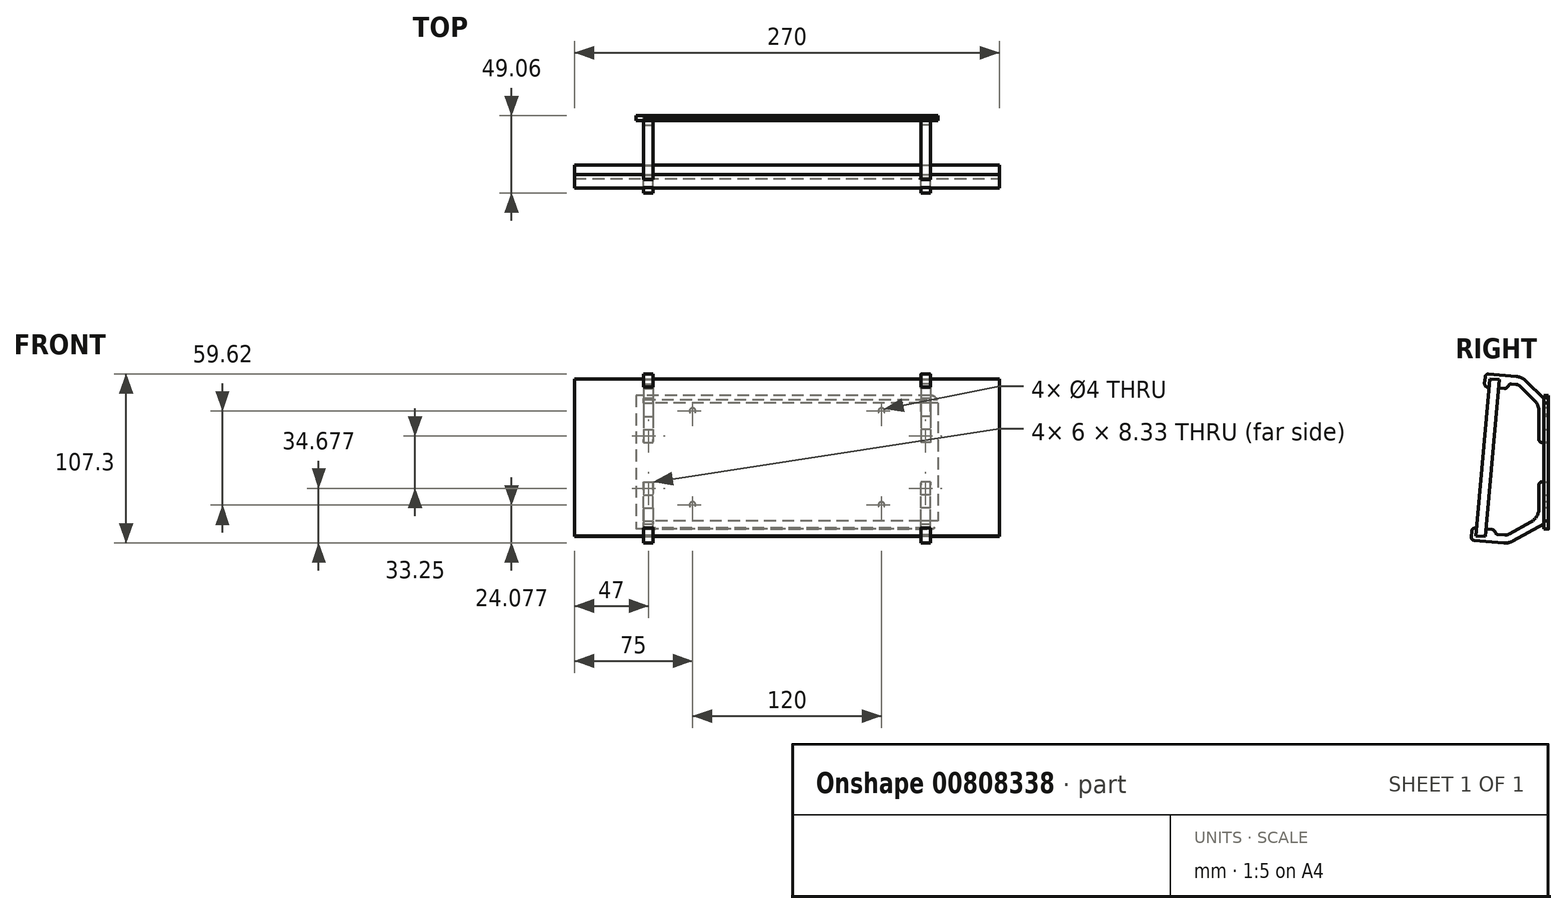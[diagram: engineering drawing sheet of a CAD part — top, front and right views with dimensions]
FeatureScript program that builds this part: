
annotation { "Feature Type Name" : "Feature", "Feature Type Description" : "" }
export const myFeature = defineFeature(function(context is Context, id is Id, definition is map)
    precondition{}
    {
        {
            var Q0;
            Q0=qCreatedBy(makeId("Front.planeOp"),FACE);
            var sketch = newSketch(context, id + "F0", { "sketchPlane" : qUnion([Q0])});
            skLineSegment(sketch, "E0", {"start": v(-49.98, 0) * mm, "end": v(35.18, 0) * mm});
            skSolve(sketch);
        }
        {
            var Q0;
            Q0=qCreatedBy(makeId("Front.planeOp"),FACE);
            var Q1;
            Q1=sQuery(id+"F0.wireOp",EDGE,"E0");
            cPlane(context, id + "F1", {"entities" : qUnion([Q0, Q1]), "cplaneType" : CPlaneType.LINE_ANGLE, "offset" : 25 * mm, "angle" : 5 * degree, "oppositeDirection" : true, "width" : 150 * mm, "height" : 150 * mm});
        }
        {
            var Q0;
            Q0=qCreatedBy(id+"F1.planeOp",FACE);
            var sketch = newSketch(context, id + "F2", { "sketchPlane" : qUnion([Q0])});
            skLineSegment(sketch, "E1.bottom", {"start": v(135, 50) * mm, "end": v(-135, 50) * mm});
            skLineSegment(sketch, "E1.top", {"start": v(135, -50) * mm, "end": v(-135, -50) * mm});
            skLineSegment(sketch, "E1.left", {"start": v(135, 50) * mm, "end": v(135, -50) * mm});
            skLineSegment(sketch, "E1.right", {"start": v(-135, 50) * mm, "end": v(-135, -50) * mm});
            skPoint(sketch, "E1.middle", {"position": v(0, 0) * mm});
            skSolve(sketch);
        }
        {
            var Q0;
            Q0=makeQuery(id+"F2.imprint","IMPRINT",FACE,{"disambiguationData":[TD([[makeQuery(id+"F2.imprint","IMPRINT",EDGE,{"derivedFrom":sQuery(id+"F2.wireOp",EDGE,"E1.bottom")}),1.0]])]});
            extrude(context, id + "F3", {"entities" : qUnion([Q0]), "depth" : 6 * mm, "offsetDistance" : 25 * mm});
        }
        {
            var Q0;
            Q0=makeQuery(id+"F3.opExtrude","SWEPT_FACE",FACE,{"disambiguationData":[OSD([sQuery(id+"F2.wireOp",EDGE,"E1.left")])]});
            cPlane(context, id + "F4", {"entities" : qUnion([Q0]), "cplaneType" : CPlaneType.OFFSET, "offset" : 50 * mm, "oppositeDirection" : true, "width" : 150 * mm, "height" : 150 * mm});
        }
        {
            var Q0;
            Q0=qCreatedBy(id+"F4.planeOp",FACE);
            var sketch = newSketch(context, id + "F5", { "sketchPlane" : qUnion([Q0])});
            skLineSegment(sketch, "E2", {"start": v(-0.9, 44.8) * mm, "end": v(-3.9, 44.55) * mm});
            skLineSegment(sketch, "E3", {"start": v(-10.33, 49.29) * mm, "end": v(-9.87, 44.03) * mm});
            skLineSegment(sketch, "E4", {"start": v(-10.33, 49.29) * mm, "end": v(-4.36, 49.8) * mm});
            skLineSegment(sketch, "E5", {"start": v(-4.36, 49.8) * mm, "end": v(-3.9, 44.55) * mm});
            skLineSegment(sketch, "E6", {"start": v(-0.9, 44.8) * mm, "end": v(-1.63, 53.06) * mm});
            skLineSegment(sketch, "E7", {"start": v(-9.87, 44.03) * mm, "end": v(-14.86, 43.59) * mm});
            skLineSegment(sketch, "E8", {"start": v(-14.86, 43.59) * mm, "end": v(-17.03, 46.7) * mm});
            skLineSegment(sketch, "E9", {"start": v(-1.63, 53.06) * mm, "end": v(-21.25, 51.34) * mm});
            skLineSegment(sketch, "E10", {"start": v(-27.43, 48.47) * mm, "end": v(-41.62, 34.35) * mm});
            skPoint(sketch, "E11.visualSharp", {"position": v(-24.86, 51.03) * mm});
            skArc(sketch, "E11.filletArc", {"start": v(-21.25, 51.34) * mm, "mid": v(-24.6, 50.45) * mm, "end": v(-27.43, 48.47) * mm});
            skLineSegment(sketch, "E12.0", {"start": v(-23.9, 44.93) * mm, "end": v(-35.62, 33.27) * mm});
            skArc(sketch, "E12.1", {"start": v(-20.82, 46.36) * mm, "mid": v(-22.49, 45.92) * mm, "end": v(-23.9, 44.93) * mm});
            skLineSegment(sketch, "E13", {"start": v(-20.82, 46.36) * mm, "end": v(-17.03, 46.7) * mm});
            skLineSegment(sketch, "E14", {"start": v(3.94, -45.07) * mm, "end": v(4.36, -49.8) * mm});
            skLineSegment(sketch, "E15", {"start": v(4.36, -49.8) * mm, "end": v(-1.62, -50.33) * mm});
            skLineSegment(sketch, "E16", {"start": v(-1.62, -50.33) * mm, "end": v(-2.03, -45.6) * mm});
            skLineSegment(sketch, "E17", {"start": v(3.94, -45.07) * mm, "end": v(6.93, -44.8) * mm});
            skLineSegment(sketch, "E18", {"start": v(6.93, -44.8) * mm, "end": v(7.6, -52.54) * mm});
            skLineSegment(sketch, "E19", {"start": v(7.6, -52.54) * mm, "end": v(-13.4, -54.38) * mm});
            skLineSegment(sketch, "E20", {"start": v(-19.16, -53.14) * mm, "end": v(-41.62, -40.57) * mm});
            skLineSegment(sketch, "E21", {"start": v(-2.03, -45.6) * mm, "end": v(-7.01, -46.03) * mm});
            skPoint(sketch, "E22.visualSharp", {"position": v(-16.47, -54.64) * mm});
            skArc(sketch, "E22.filletArc", {"start": v(-19.16, -53.14) * mm, "mid": v(-16.37, -54.2) * mm, "end": v(-13.4, -54.38) * mm});
            skArc(sketch, "E23.0", {"start": v(-16.72, -48.78) * mm, "mid": v(-15.32, -49.3) * mm, "end": v(-13.84, -49.4) * mm});
            skLineSegment(sketch, "E23.1", {"start": v(-16.72, -48.78) * mm, "end": v(-35.62, -38.2) * mm});
            skLineSegment(sketch, "E24", {"start": v(-7.01, -46.03) * mm, "end": v(-8.36, -48.91) * mm});
            skLineSegment(sketch, "E25", {"start": v(-13.84, -49.4) * mm, "end": v(-8.36, -48.91) * mm});
            skLineSegment(sketch, "E26", {"start": v(-35.62, 33.27) * mm, "end": v(-35.62, 9.35) * mm});
            skLineSegment(sketch, "E27", {"start": v(-35.62, 9.35) * mm, "end": v(-41.62, 9.35) * mm});
            skLineSegment(sketch, "E28", {"start": v(-35.62, -38.2) * mm, "end": v(-35.62, -15.57) * mm});
            skLineSegment(sketch, "E29", {"start": v(-35.62, -15.57) * mm, "end": v(-41.62, -15.57) * mm});
            skLineSegment(sketch, "E30", {"start": v(-41.62, 34.35) * mm, "end": v(-41.62, 26.02) * mm});
            skLineSegment(sketch, "E31", {"start": v(-41.62, 26.02) * mm, "end": v(-38.62, 26.02) * mm});
            skLineSegment(sketch, "E32", {"start": v(-38.62, 26.02) * mm, "end": v(-38.62, 17.68) * mm});
            skLineSegment(sketch, "E33", {"start": v(-38.62, 17.68) * mm, "end": v(-41.62, 17.68) * mm});
            skLineSegment(sketch, "E34", {"start": v(-41.62, 17.68) * mm, "end": v(-41.62, 9.35) * mm});
            skLineSegment(sketch, "E35", {"start": v(-41.62, -40.57) * mm, "end": v(-41.62, -32.23) * mm});
            skLineSegment(sketch, "E36", {"start": v(-41.62, -32.23) * mm, "end": v(-38.62, -32.23) * mm});
            skLineSegment(sketch, "E37", {"start": v(-38.62, -32.23) * mm, "end": v(-38.62, -23.9) * mm});
            skLineSegment(sketch, "E38", {"start": v(-38.62, -23.9) * mm, "end": v(-41.62, -23.9) * mm});
            skLineSegment(sketch, "E39", {"start": v(-41.62, -23.9) * mm, "end": v(-41.62, -15.57) * mm});
            skSolve(sketch);
        }
        {
            var Q0;
            Q0=makeQuery(id+"F5.imprint","IMPRINT",FACE,{"disambiguationData":[TD([[makeQuery(id+"F5.imprint","IMPRINT",EDGE,{"derivedFrom":sQuery(id+"F5.wireOp",EDGE,"E2")}),-1.0]])]});
            var Q1;
            Q1=makeQuery(id+"F5.imprint","IMPRINT",FACE,{"disambiguationData":[TD([[makeQuery(id+"F5.imprint","IMPRINT",EDGE,{"derivedFrom":sQuery(id+"F5.wireOp",EDGE,"E14")}),1.0]])]});
            extrude(context, id + "F6", {"entities" : qUnion([Q0, Q1]), "depth" : 6 * mm, "offsetDistance" : 25 * mm});
        }
        {
            var Q0;
            Q0=makeQuery(id+"F6.opExtrude","SWEPT_BODY",BODY,{"disambiguationData":[OSD([sQuery(id+"F5.wireOp",EDGE,"E2"),sQuery(id+"F5.wireOp",EDGE,"E3"),sQuery(id+"F5.wireOp",EDGE,"E4"),sQuery(id+"F5.wireOp",EDGE,"E5"),sQuery(id+"F5.wireOp",EDGE,"E6"),sQuery(id+"F5.wireOp",EDGE,"E7"),sQuery(id+"F5.wireOp",EDGE,"E8"),sQuery(id+"F5.wireOp",EDGE,"E9"),sQuery(id+"F5.wireOp",EDGE,"E10"),sQuery(id+"F5.wireOp",EDGE,"E11.filletArc"),sQuery(id+"F5.wireOp",EDGE,"E12.0"),sQuery(id+"F5.wireOp",EDGE,"E12.1"),sQuery(id+"F5.wireOp",EDGE,"E13"),sQuery(id+"F5.wireOp",EDGE,"E26"),sQuery(id+"F5.wireOp",EDGE,"E27"),sQuery(id+"F5.wireOp",EDGE,"E30"),sQuery(id+"F5.wireOp",EDGE,"E31"),sQuery(id+"F5.wireOp",EDGE,"E32"),sQuery(id+"F5.wireOp",EDGE,"E33"),sQuery(id+"F5.wireOp",EDGE,"E34")])]});
            var Q1;
            Q1=makeQuery(id+"F6.opExtrude","SWEPT_BODY",BODY,{"disambiguationData":[OSD([sQuery(id+"F5.wireOp",EDGE,"E14"),sQuery(id+"F5.wireOp",EDGE,"E15"),sQuery(id+"F5.wireOp",EDGE,"E16"),sQuery(id+"F5.wireOp",EDGE,"E17"),sQuery(id+"F5.wireOp",EDGE,"E18"),sQuery(id+"F5.wireOp",EDGE,"E19"),sQuery(id+"F5.wireOp",EDGE,"E20"),sQuery(id+"F5.wireOp",EDGE,"E21"),sQuery(id+"F5.wireOp",EDGE,"E22.filletArc"),sQuery(id+"F5.wireOp",EDGE,"E23.0"),sQuery(id+"F5.wireOp",EDGE,"E23.1"),sQuery(id+"F5.wireOp",EDGE,"E24"),sQuery(id+"F5.wireOp",EDGE,"E25"),sQuery(id+"F5.wireOp",EDGE,"E28"),sQuery(id+"F5.wireOp",EDGE,"E29"),sQuery(id+"F5.wireOp",EDGE,"E35"),sQuery(id+"F5.wireOp",EDGE,"E36"),sQuery(id+"F5.wireOp",EDGE,"E37"),sQuery(id+"F5.wireOp",EDGE,"E38"),sQuery(id+"F5.wireOp",EDGE,"E39")])]});
            var Q2;
            Q2=qCreatedBy(makeId("Right.planeOp"),FACE);
            mirror(context, id + "F7", {"entities" : qUnion([Q0, Q1]), "mirrorPlane" : qUnion([Q2])});
        }
        {
            var Q0;
            Q0=makeQuery(id+"F7.opPattern","COPY",EDGE,{"derivedFrom":makeQuery(id+"F6.opExtrude","SWEPT_EDGE",EDGE,{"disambiguationData":[OSD([sQuery(id+"F5.wireOp",EDGE,"E12.0"),sQuery(id+"F5.wireOp",EDGE,"E26")])]}),"instanceName":"1"});
            var Q1;
            Q1=makeQuery(id+"F6.opExtrude","SWEPT_EDGE",EDGE,{"disambiguationData":[OSD([sQuery(id+"F5.wireOp",EDGE,"E12.0"),sQuery(id+"F5.wireOp",EDGE,"E26")])]});
            var Q2;
            Q2=makeQuery(id+"F6.opExtrude","SWEPT_EDGE",EDGE,{"disambiguationData":[OSD([sQuery(id+"F5.wireOp",EDGE,"E23.1"),sQuery(id+"F5.wireOp",EDGE,"E28")])]});
            var Q3;
            Q3=makeQuery(id+"F7.opPattern","COPY",EDGE,{"derivedFrom":makeQuery(id+"F6.opExtrude","SWEPT_EDGE",EDGE,{"disambiguationData":[OSD([sQuery(id+"F5.wireOp",EDGE,"E23.1"),sQuery(id+"F5.wireOp",EDGE,"E28")])]}),"instanceName":"1"});
            fillet(context, id + "F8", {"entities" : qUnion([Q0, Q1, Q2, Q3]), "radius" : 10 * mm, "tangentPropagation" : true, "allowEdgeOverflow" : false});
        }
        {
            var Q0;
            Q0=makeQuery(id+"F6.opExtrude","SWEPT_EDGE",EDGE,{"disambiguationData":[OSD([sQuery(id+"F5.wireOp",EDGE,"E28"),sQuery(id+"F5.wireOp",EDGE,"E29")])]});
            var Q1;
            Q1=makeQuery(id+"F6.opExtrude","SWEPT_EDGE",EDGE,{"disambiguationData":[OSD([sQuery(id+"F5.wireOp",EDGE,"E17"),sQuery(id+"F5.wireOp",EDGE,"E18")])]});
            var Q2;
            Q2=makeQuery(id+"F6.opExtrude","SWEPT_EDGE",EDGE,{"disambiguationData":[OSD([sQuery(id+"F5.wireOp",EDGE,"E18"),sQuery(id+"F5.wireOp",EDGE,"E19")])]});
            var Q3;
            Q3=makeQuery(id+"F6.opExtrude","SWEPT_EDGE",EDGE,{"disambiguationData":[OSD([sQuery(id+"F5.wireOp",EDGE,"E24"),sQuery(id+"F5.wireOp",EDGE,"E25")])]});
            var Q4;
            Q4=makeQuery(id+"F6.opExtrude","SWEPT_EDGE",EDGE,{"disambiguationData":[OSD([sQuery(id+"F5.wireOp",EDGE,"E21"),sQuery(id+"F5.wireOp",EDGE,"E24")])]});
            var Q5;
            Q5=makeQuery(id+"F7.opPattern","COPY",EDGE,{"derivedFrom":makeQuery(id+"F6.opExtrude","SWEPT_EDGE",EDGE,{"disambiguationData":[OSD([sQuery(id+"F5.wireOp",EDGE,"E21"),sQuery(id+"F5.wireOp",EDGE,"E24")])]}),"instanceName":"1"});
            var Q6;
            Q6=makeQuery(id+"F7.opPattern","COPY",EDGE,{"derivedFrom":makeQuery(id+"F6.opExtrude","SWEPT_EDGE",EDGE,{"disambiguationData":[OSD([sQuery(id+"F5.wireOp",EDGE,"E24"),sQuery(id+"F5.wireOp",EDGE,"E25")])]}),"instanceName":"1"});
            var Q7;
            Q7=makeQuery(id+"F7.opPattern","COPY",EDGE,{"derivedFrom":makeQuery(id+"F6.opExtrude","SWEPT_EDGE",EDGE,{"disambiguationData":[OSD([sQuery(id+"F5.wireOp",EDGE,"E28"),sQuery(id+"F5.wireOp",EDGE,"E29")])]}),"instanceName":"1"});
            var Q8;
            Q8=makeQuery(id+"F6.opExtrude","SWEPT_EDGE",EDGE,{"disambiguationData":[OSD([sQuery(id+"F5.wireOp",EDGE,"E26"),sQuery(id+"F5.wireOp",EDGE,"E27")])]});
            var Q9;
            Q9=makeQuery(id+"F7.opPattern","COPY",EDGE,{"derivedFrom":makeQuery(id+"F6.opExtrude","SWEPT_EDGE",EDGE,{"disambiguationData":[OSD([sQuery(id+"F5.wireOp",EDGE,"E26"),sQuery(id+"F5.wireOp",EDGE,"E27")])]}),"instanceName":"1"});
            var Q10;
            Q10=makeQuery(id+"F6.opExtrude","SWEPT_EDGE",EDGE,{"disambiguationData":[OSD([sQuery(id+"F5.wireOp",EDGE,"E6"),sQuery(id+"F5.wireOp",EDGE,"E9")])]});
            var Q11;
            Q11=makeQuery(id+"F6.opExtrude","SWEPT_EDGE",EDGE,{"disambiguationData":[OSD([sQuery(id+"F5.wireOp",EDGE,"E2"),sQuery(id+"F5.wireOp",EDGE,"E6")])]});
            var Q12;
            Q12=makeQuery(id+"F7.opPattern","COPY",EDGE,{"derivedFrom":makeQuery(id+"F6.opExtrude","SWEPT_EDGE",EDGE,{"disambiguationData":[OSD([sQuery(id+"F5.wireOp",EDGE,"E6"),sQuery(id+"F5.wireOp",EDGE,"E9")])]}),"instanceName":"1"});
            var Q13;
            Q13=makeQuery(id+"F7.opPattern","COPY",EDGE,{"derivedFrom":makeQuery(id+"F6.opExtrude","SWEPT_EDGE",EDGE,{"disambiguationData":[OSD([sQuery(id+"F5.wireOp",EDGE,"E2"),sQuery(id+"F5.wireOp",EDGE,"E6")])]}),"instanceName":"1"});
            var Q14;
            Q14=makeQuery(id+"F7.opPattern","COPY",EDGE,{"derivedFrom":makeQuery(id+"F6.opExtrude","SWEPT_EDGE",EDGE,{"disambiguationData":[OSD([sQuery(id+"F5.wireOp",EDGE,"E17"),sQuery(id+"F5.wireOp",EDGE,"E18")])]}),"instanceName":"1"});
            var Q15;
            Q15=makeQuery(id+"F7.opPattern","COPY",EDGE,{"derivedFrom":makeQuery(id+"F6.opExtrude","SWEPT_EDGE",EDGE,{"disambiguationData":[OSD([sQuery(id+"F5.wireOp",EDGE,"E18"),sQuery(id+"F5.wireOp",EDGE,"E19")])]}),"instanceName":"1"});
            var Q16;
            Q16=makeQuery(id+"F7.opPattern","COPY",EDGE,{"derivedFrom":makeQuery(id+"F6.opExtrude","SWEPT_EDGE",EDGE,{"disambiguationData":[OSD([sQuery(id+"F5.wireOp",EDGE,"E8"),sQuery(id+"F5.wireOp",EDGE,"E13")])]}),"instanceName":"1"});
            var Q17;
            Q17=makeQuery(id+"F7.opPattern","COPY",EDGE,{"derivedFrom":makeQuery(id+"F6.opExtrude","SWEPT_EDGE",EDGE,{"disambiguationData":[OSD([sQuery(id+"F5.wireOp",EDGE,"E7"),sQuery(id+"F5.wireOp",EDGE,"E8")])]}),"instanceName":"1"});
            var Q18;
            Q18=makeQuery(id+"F6.opExtrude","SWEPT_EDGE",EDGE,{"disambiguationData":[OSD([sQuery(id+"F5.wireOp",EDGE,"E8"),sQuery(id+"F5.wireOp",EDGE,"E13")])]});
            var Q19;
            Q19=makeQuery(id+"F6.opExtrude","SWEPT_EDGE",EDGE,{"disambiguationData":[OSD([sQuery(id+"F5.wireOp",EDGE,"E7"),sQuery(id+"F5.wireOp",EDGE,"E8")])]});
            fillet(context, id + "F9", {"entities" : qUnion([Q0, Q1, Q2, Q3, Q4, Q5, Q6, Q7, Q8, Q9, Q10, Q11, Q12, Q13, Q14, Q15, Q16, Q17, Q18, Q19]), "radius" : 2 * mm, "tangentPropagation" : true, "allowEdgeOverflow" : false});
        }
        {
            var Q0;
            Q0=makeQuery(id+"F7.opPattern","COPY",FACE,{"derivedFrom":makeQuery(id+"F6.opExtrude","SWEPT_FACE",FACE,{"disambiguationData":[OSD([sQuery(id+"F5.wireOp",EDGE,"E32")])]}),"instanceName":"1"});
            var sketch = newSketch(context, id + "F10", { "sketchPlane" : qUnion([Q0])});
            skLineSegment(sketch, "E40.bottom", {"start": v(-96, 39.35) * mm, "end": v(96, 39.35) * mm});
            skLineSegment(sketch, "E40.top", {"start": v(-96, -45.57) * mm, "end": v(96, -45.57) * mm});
            skLineSegment(sketch, "E40.left", {"start": v(-96, 39.35) * mm, "end": v(-96, -45.57) * mm});
            skLineSegment(sketch, "E40.right", {"start": v(96, 39.35) * mm, "end": v(96, -45.57) * mm});
            skLineSegment(sketch, "E41.bottom", {"start": v(-91, 34.35) * mm, "end": v(-85, 34.35) * mm});
            skLineSegment(sketch, "E41.top", {"start": v(-91, 26.02) * mm, "end": v(-85, 26.02) * mm});
            skLineSegment(sketch, "E41.left", {"start": v(-91, 34.35) * mm, "end": v(-91, 26.02) * mm});
            skLineSegment(sketch, "E41.right", {"start": v(-85, 34.35) * mm, "end": v(-85, 26.02) * mm});
            skLineSegment(sketch, "E42.bottom", {"start": v(-91, 17.68) * mm, "end": v(-85, 17.68) * mm});
            skLineSegment(sketch, "E42.top", {"start": v(-91, 9.35) * mm, "end": v(-85, 9.35) * mm});
            skLineSegment(sketch, "E42.left", {"start": v(-91, 17.68) * mm, "end": v(-91, 9.35) * mm});
            skLineSegment(sketch, "E42.right", {"start": v(-85, 17.68) * mm, "end": v(-85, 9.35) * mm});
            skLineSegment(sketch, "E43.bottom", {"start": v(-91, -15.57) * mm, "end": v(-85, -15.57) * mm});
            skLineSegment(sketch, "E43.top", {"start": v(-91, -23.9) * mm, "end": v(-85, -23.9) * mm});
            skLineSegment(sketch, "E43.left", {"start": v(-91, -15.57) * mm, "end": v(-91, -23.9) * mm});
            skLineSegment(sketch, "E43.right", {"start": v(-85, -15.57) * mm, "end": v(-85, -23.9) * mm});
            skLineSegment(sketch, "E44.bottom", {"start": v(-91, -32.23) * mm, "end": v(-85, -32.23) * mm});
            skLineSegment(sketch, "E44.top", {"start": v(-91, -40.57) * mm, "end": v(-85, -40.57) * mm});
            skLineSegment(sketch, "E44.left", {"start": v(-91, -32.23) * mm, "end": v(-91, -40.57) * mm});
            skLineSegment(sketch, "E44.right", {"start": v(-85, -32.23) * mm, "end": v(-85, -40.57) * mm});
            skLineSegment(sketch, "E45", {"start": v(0, 0) * mm, "end": v(0, 26.9) * mm, "construction": true});
            skLineSegment(sketch, "E46.MirrorCS", {"start": v(85, 34.35) * mm, "end": v(85, 26.02) * mm});
            skLineSegment(sketch, "E47.MirrorCS", {"start": v(91, 34.35) * mm, "end": v(85, 34.35) * mm});
            skLineSegment(sketch, "E48.MirrorCS", {"start": v(91, 26.02) * mm, "end": v(85, 26.02) * mm});
            skLineSegment(sketch, "E49.MirrorCS", {"start": v(91, 34.35) * mm, "end": v(91, 26.02) * mm});
            skLineSegment(sketch, "E50.MirrorCS", {"start": v(91, -15.57) * mm, "end": v(91, -23.9) * mm});
            skLineSegment(sketch, "E51.MirrorCS", {"start": v(96, 39.35) * mm, "end": v(-96, 39.35) * mm});
            skLineSegment(sketch, "E52.MirrorCS", {"start": v(96, -45.57) * mm, "end": v(-96, -45.57) * mm});
            skLineSegment(sketch, "E53.MirrorCS", {"start": v(85, -32.23) * mm, "end": v(85, -40.57) * mm});
            skLineSegment(sketch, "E54.MirrorCS", {"start": v(91, -32.23) * mm, "end": v(85, -32.23) * mm});
            skLineSegment(sketch, "E55.MirrorCS", {"start": v(85, -15.57) * mm, "end": v(85, -23.9) * mm});
            skLineSegment(sketch, "E56.MirrorCS", {"start": v(91, -23.9) * mm, "end": v(85, -23.9) * mm});
            skLineSegment(sketch, "E57.MirrorCS", {"start": v(91, -32.23) * mm, "end": v(91, -40.57) * mm});
            skLineSegment(sketch, "E58.MirrorCS", {"start": v(91, -15.57) * mm, "end": v(85, -15.57) * mm});
            skLineSegment(sketch, "E59.MirrorCS", {"start": v(85, 17.68) * mm, "end": v(85, 9.35) * mm});
            skLineSegment(sketch, "E60.MirrorCS", {"start": v(91, 17.68) * mm, "end": v(91, 9.35) * mm});
            skLineSegment(sketch, "E61.MirrorCS", {"start": v(91, -40.57) * mm, "end": v(85, -40.57) * mm});
            skLineSegment(sketch, "E62.MirrorCS", {"start": v(91, 9.35) * mm, "end": v(85, 9.35) * mm});
            skLineSegment(sketch, "E63.MirrorCS", {"start": v(91, 17.68) * mm, "end": v(85, 17.68) * mm});
            skCircle(sketch, "E64", {"center": v(-60, 29.29) * mm, "radius": 2 * mm});
            skCircle(sketch, "E65", {"center": v(-60, -30.33) * mm, "radius": 2 * mm});
            skCircle(sketch, "E66.MirrorC", {"center": v(60, -30.33) * mm, "radius": 2 * mm});
            skCircle(sketch, "E67.MirrorC", {"center": v(60, 29.29) * mm, "radius": 2 * mm});
            skSolve(sketch);
        }
        {
            var Q0;
            Q0 = qSketchRegion(id + "F10", true);
            extrude(context, id + "F11", {"entities" : qUnion([Q0]), "depth" : 3 * mm, "offsetDistance" : 25 * mm});
        }
        {
            var Q0;
            Q0=makeQuery(id+"F11.opExtrude","SWEPT_EDGE",EDGE,{"disambiguationData":[OSD([sQuery(id+"F10.wireOp",EDGE,"E40.left"),sQuery(id+"F10.wireOp",EDGE,"E51.MirrorCS")])]});
            var Q1;
            Q1=makeQuery(id+"F11.opExtrude","SWEPT_EDGE",EDGE,{"disambiguationData":[OSD([sQuery(id+"F10.wireOp",EDGE,"E40.left"),sQuery(id+"F10.wireOp",EDGE,"E52.MirrorCS")])]});
            var Q2;
            Q2=makeQuery(id+"F11.opExtrude","SWEPT_EDGE",EDGE,{"disambiguationData":[OSD([sQuery(id+"F10.wireOp",EDGE,"E52.MirrorCS"),sQuery(id+"F10.wireOp",EDGE,"E40.right")])]});
            var Q3;
            Q3=makeQuery(id+"F11.opExtrude","SWEPT_EDGE",EDGE,{"disambiguationData":[OSD([sQuery(id+"F10.wireOp",EDGE,"E51.MirrorCS"),sQuery(id+"F10.wireOp",EDGE,"E40.right")])]});
            fillet(context, id + "F12", {"entities" : qUnion([Q0, Q1, Q2, Q3]), "radius" : 5 * mm, "tangentPropagation" : true, "allowEdgeOverflow" : false});
        }
        {
            var Q0;
            Q0=makeQuery(id+"F6.opExtrude","CAP_FACE",FACE,{"disambiguationData":[OSD([sQuery(id+"F5.wireOp",EDGE,"E2"),sQuery(id+"F5.wireOp",EDGE,"E3"),sQuery(id+"F5.wireOp",EDGE,"E4"),sQuery(id+"F5.wireOp",EDGE,"E5"),sQuery(id+"F5.wireOp",EDGE,"E6"),sQuery(id+"F5.wireOp",EDGE,"E7"),sQuery(id+"F5.wireOp",EDGE,"E8"),sQuery(id+"F5.wireOp",EDGE,"E9"),sQuery(id+"F5.wireOp",EDGE,"E10"),sQuery(id+"F5.wireOp",EDGE,"E11.filletArc"),sQuery(id+"F5.wireOp",EDGE,"E12.0"),sQuery(id+"F5.wireOp",EDGE,"E12.1"),sQuery(id+"F5.wireOp",EDGE,"E13"),sQuery(id+"F5.wireOp",EDGE,"E26"),sQuery(id+"F5.wireOp",EDGE,"E27"),sQuery(id+"F5.wireOp",EDGE,"E30"),sQuery(id+"F5.wireOp",EDGE,"E31"),sQuery(id+"F5.wireOp",EDGE,"E32"),sQuery(id+"F5.wireOp",EDGE,"E33"),sQuery(id+"F5.wireOp",EDGE,"E34")])],"isStart":false});
            var sketch = newSketch(context, id + "F13", { "sketchPlane" : qUnion([Q0])});
            skLineSegment(sketch, "E68", {"start": v(-43.43, 34.35) * mm, "end": v(-38.62, 34.35) * mm});
            skLineSegment(sketch, "E69", {"start": v(-38.62, 34.35) * mm, "end": v(-38.62, 40.4) * mm});
            skLineSegment(sketch, "E70", {"start": v(-38.62, 40.4) * mm, "end": v(-43.43, 34.35) * mm});
            skLineSegment(sketch, "E71", {"start": v(-45.01, -40.57) * mm, "end": v(-38.62, -40.57) * mm});
            skLineSegment(sketch, "E72", {"start": v(-38.62, -40.57) * mm, "end": v(-38.62, -48.27) * mm});
            skLineSegment(sketch, "E73", {"start": v(-38.62, -48.27) * mm, "end": v(-45.01, -40.57) * mm});
            skSolve(sketch);
        }
        {
            var Q0;
            Q0 = qSketchRegion(id + "F13", true);
            extrude(context, id + "F14", {"entities" : qUnion([Q0]), "operationType" : NewBodyOperationType.REMOVE, "oppositeDirection" : true, "depth" : 703 * mm, "offsetDistance" : 25 * mm});
        }
    });
